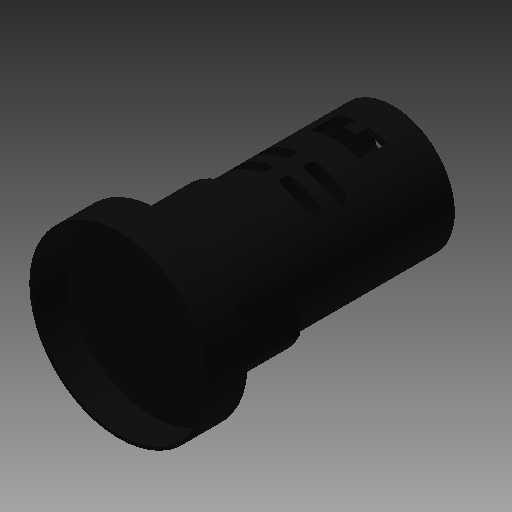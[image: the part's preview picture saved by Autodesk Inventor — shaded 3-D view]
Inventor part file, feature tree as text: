
AUTODESK INVENTOR PART (.ipt)
format: ipt  version: 2017 (Build 210142000, 142)  size: 256,512 bytes
history: native  units: in
note: dims shown in document units (in); Inventor stores cm internally (conversion verified against a paired STEP export)
features: other x2, sketch x2, imported_body x1
ambient origin geometry x8: Origin, YZ Plane, XZ Plane, XY Plane, X Axis, Y Axis, Z Axis, Center Point
bodies: Body1 (feature_tree)
feature tree (5):
  other  "Cut-Extrude1"
  other  "light panel.ipt1"
  sketch  "Sketch1"
  sketch  "Sketch2"
  imported_body  "Base1"
